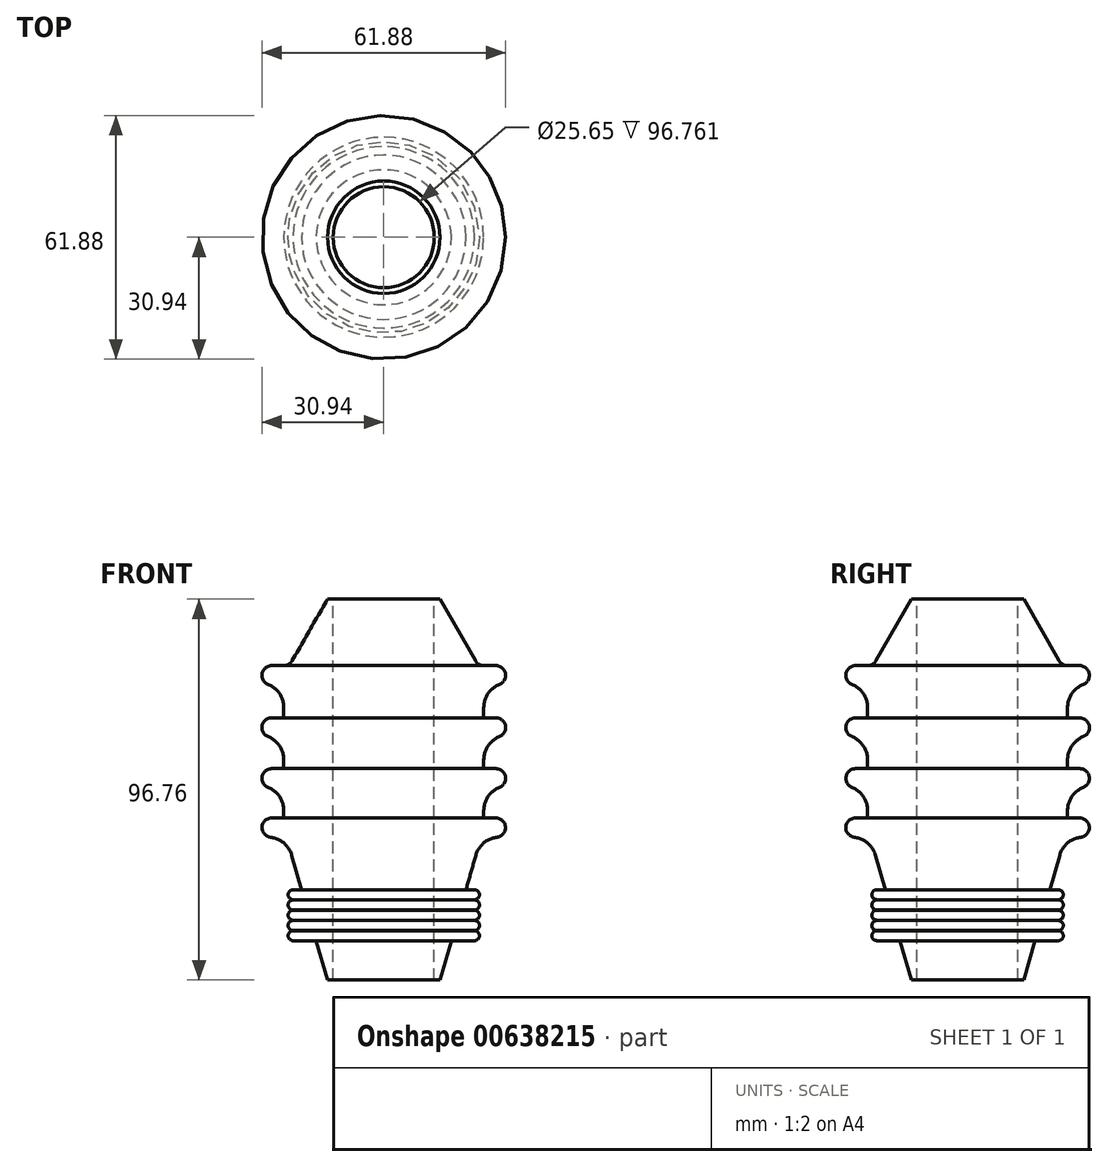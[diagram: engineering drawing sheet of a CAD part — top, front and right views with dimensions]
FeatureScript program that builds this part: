
annotation { "Feature Type Name" : "Feature", "Feature Type Description" : "" }
export const myFeature = defineFeature(function(context is Context, id is Id, definition is map)
    precondition{}
    {
        {
            var Q0;
            Q0=qCreatedBy(makeId("Front.planeOp"),FACE);
            var sketch = newSketch(context, id + "F0", { "sketchPlane" : qUnion([Q0])});
            skLineSegment(sketch, "E0", {"start": v(0, 0) * mm, "end": v(0, 96.76) * mm});
            skLineSegment(sketch, "E1", {"start": v(0, 96.76) * mm, "end": v(0, 58.06) * mm});
            skLineSegment(sketch, "E2", {"start": v(0, 0) * mm, "end": v(0, 38.7) * mm});
            skLineSegment(sketch, "E3", {"start": v(0, 96.76) * mm, "end": v(-14.29, 96.76) * mm});
            skLineSegment(sketch, "E4", {"start": v(-14.29, 96.76) * mm, "end": v(-14.29, 0) * mm});
            skLineSegment(sketch, "E5", {"start": v(-14.29, 0) * mm, "end": v(0, 0) * mm});
            skLineSegment(sketch, "E6", {"start": v(0, 96.76) * mm, "end": v(0, 77.4) * mm});
            skLineSegment(sketch, "E7", {"start": v(-25.4, 77.4) * mm, "end": v(-25.4, 38.7) * mm});
            skLineSegment(sketch, "E8", {"start": v(-25.4, 77.4) * mm, "end": v(-14.29, 96.76) * mm});
            skLineSegment(sketch, "E9", {"start": v(-25.4, 38.7) * mm, "end": v(-14.29, 0) * mm});
            skLineSegment(sketch, "E10", {"start": v(-25.4, 77.4) * mm, "end": v(-25.4, 64.14) * mm});
            skLineSegment(sketch, "E11", {"start": v(-25.4, 64.14) * mm, "end": v(-25.4, 51.24) * mm});
            skLineSegment(sketch, "E12", {"start": v(-25.4, 77.4) * mm, "end": v(-25.4, 74.95) * mm});
            skLineSegment(sketch, "E13", {"start": v(-25.4, 77.4) * mm, "end": v(-25.4, 79.87) * mm});
            skLineSegment(sketch, "E14", {"start": v(-25.4, 79.87) * mm, "end": v(0, 79.87) * mm});
            skLineSegment(sketch, "E15", {"start": v(-25.4, 64.14) * mm, "end": v(-25.4, 66.6) * mm});
            skLineSegment(sketch, "E16", {"start": v(-25.4, 64.14) * mm, "end": v(-25.4, 61.68) * mm});
            skLineSegment(sketch, "E17", {"start": v(-25.4, 61.68) * mm, "end": v(0, 61.68) * mm});
            skLineSegment(sketch, "E18", {"start": v(-25.4, 66.6) * mm, "end": v(0, 66.6) * mm});
            skLineSegment(sketch, "E19", {"start": v(-25.4, 74.95) * mm, "end": v(0, 74.95) * mm});
            skLineSegment(sketch, "E20", {"start": v(-25.4, 51.24) * mm, "end": v(-25.4, 53.7) * mm});
            skLineSegment(sketch, "E21", {"start": v(-25.4, 51.24) * mm, "end": v(-25.4, 48.77) * mm});
            skLineSegment(sketch, "E22", {"start": v(-25.4, 48.77) * mm, "end": v(0, 48.77) * mm});
            skLineSegment(sketch, "E23", {"start": v(-25.4, 53.7) * mm, "end": v(0, 53.7) * mm});
            skLineSegment(sketch, "E24", {"start": v(-25.4, 38.7) * mm, "end": v(-25.4, 41.17) * mm});
            skLineSegment(sketch, "E25", {"start": v(-25.4, 38.7) * mm, "end": v(-25.4, 36.24) * mm});
            skLineSegment(sketch, "E26", {"start": v(-25.4, 36.24) * mm, "end": v(0, 36.24) * mm});
            skLineSegment(sketch, "E27", {"start": v(-25.4, 41.17) * mm, "end": v(0, 41.17) * mm});
            skLineSegment(sketch, "E28", {"start": v(-25.4, 79.87) * mm, "end": v(-28.48, 79.87) * mm});
            skLineSegment(sketch, "E29", {"start": v(-25.4, 36.24) * mm, "end": v(-28.48, 36.24) * mm});
            skLineSegment(sketch, "E30", {"start": v(-28.48, 36.24) * mm, "end": v(-28.48, 41.17) * mm});
            skLineSegment(sketch, "E31", {"start": v(-25.4, 74.95) * mm, "end": v(-28.48, 74.95) * mm});
            skLineSegment(sketch, "E32", {"start": v(-25.4, 66.6) * mm, "end": v(-28.48, 66.6) * mm});
            skLineSegment(sketch, "E33", {"start": v(-25.4, 61.68) * mm, "end": v(-28.48, 61.68) * mm});
            skLineSegment(sketch, "E34", {"start": v(-25.4, 53.7) * mm, "end": v(-28.48, 53.7) * mm});
            skLineSegment(sketch, "E35", {"start": v(-25.4, 48.77) * mm, "end": v(-28.48, 48.77) * mm});
            skLineSegment(sketch, "E36", {"start": v(-25.4, 41.17) * mm, "end": v(-28.48, 41.17) * mm});
            skLineSegment(sketch, "E37.trimOffspring", {"start": v(-28.48, 74.95) * mm, "end": v(-28.48, 79.87) * mm});
            skLineSegment(sketch, "E38.trimOffspring", {"start": v(-28.48, 61.68) * mm, "end": v(-28.48, 66.6) * mm});
            skLineSegment(sketch, "E39.trimOffspring", {"start": v(-28.48, 48.77) * mm, "end": v(-28.48, 53.7) * mm});
            skArc(sketch, "E40", {"start": v(-28.48, 79.87) * mm, "mid": v(-30.94, 77.4) * mm, "end": v(-28.48, 74.95) * mm});
            skArc(sketch, "E41", {"start": v(-28.48, 66.6) * mm, "mid": v(-30.94, 64.14) * mm, "end": v(-28.48, 61.68) * mm});
            skArc(sketch, "E42", {"start": v(-28.48, 53.7) * mm, "mid": v(-30.94, 51.24) * mm, "end": v(-28.48, 48.77) * mm});
            skArc(sketch, "E43", {"start": v(-28.48, 41.17) * mm, "mid": v(-30.94, 38.7) * mm, "end": v(-28.48, 36.24) * mm});
            skLineSegment(sketch, "E44", {"start": v(-24.7, 36.24) * mm, "end": v(-14.29, 0) * mm});
            skLineSegment(sketch, "E45", {"start": v(-14.29, 0) * mm, "end": v(-16.02, 6.04) * mm});
            skLineSegment(sketch, "E46", {"start": v(-24.7, 36.24) * mm, "end": v(-18.26, 13.85) * mm});
            skLineSegment(sketch, "E47", {"start": v(-16.02, 6.04) * mm, "end": v(-18.26, 13.85) * mm});
            skLineSegment(sketch, "E48", {"start": v(-18.26, 13.85) * mm, "end": v(-20.5, 21.66) * mm});
            skLineSegment(sketch, "E49", {"start": v(-20.5, 21.66) * mm, "end": v(-19.76, 19.06) * mm});
            skLineSegment(sketch, "E50", {"start": v(-19.76, 19.06) * mm, "end": v(-19.01, 16.45) * mm});
            skLineSegment(sketch, "E51", {"start": v(-19.01, 16.45) * mm, "end": v(-18.26, 13.85) * mm});
            skLineSegment(sketch, "E52", {"start": v(-18.26, 13.85) * mm, "end": v(-17.52, 11.24) * mm});
            skLineSegment(sketch, "E53", {"start": v(-17.52, 11.24) * mm, "end": v(-16.77, 8.64) * mm});
            skLineSegment(sketch, "E54", {"start": v(-16.77, 8.64) * mm, "end": v(-16.02, 6.04) * mm});
            skLineSegment(sketch, "E55", {"start": v(-20.5, 21.66) * mm, "end": v(-23.05, 21.66) * mm});
            skLineSegment(sketch, "E56", {"start": v(-23.05, 21.66) * mm, "end": v(-23.05, 9.97) * mm});
            skLineSegment(sketch, "E57", {"start": v(-17.52, 11.24) * mm, "end": v(-23.05, 11.24) * mm});
            skLineSegment(sketch, "E58", {"start": v(-23.05, 11.24) * mm, "end": v(-17.52, 11.24) * mm});
            skLineSegment(sketch, "E59", {"start": v(-18.26, 13.85) * mm, "end": v(-23.05, 13.85) * mm});
            skLineSegment(sketch, "E60", {"start": v(-23.05, 13.85) * mm, "end": v(-18.26, 13.85) * mm});
            skLineSegment(sketch, "E61", {"start": v(-19.01, 16.45) * mm, "end": v(-23.05, 16.45) * mm});
            skLineSegment(sketch, "E62", {"start": v(-23.05, 16.45) * mm, "end": v(-19.01, 16.45) * mm});
            skLineSegment(sketch, "E63", {"start": v(-19.76, 19.06) * mm, "end": v(-23.05, 19.06) * mm});
            skLineSegment(sketch, "E64", {"start": v(-23.05, 19.06) * mm, "end": v(-19.76, 19.06) * mm});
            skArc(sketch, "E65", {"start": v(-23.05, 22.93) * mm, "mid": v(-24.32, 21.66) * mm, "end": v(-23.05, 20.39) * mm});
            skArc(sketch, "E66", {"start": v(-23.05, 20.33) * mm, "mid": v(-24.32, 19.06) * mm, "end": v(-23.05, 17.79) * mm});
            skArc(sketch, "E67", {"start": v(-23.05, 17.72) * mm, "mid": v(-24.32, 16.45) * mm, "end": v(-23.05, 15.18) * mm});
            skArc(sketch, "E68", {"start": v(-23.05, 15.12) * mm, "mid": v(-24.32, 13.85) * mm, "end": v(-23.05, 12.58) * mm});
            skArc(sketch, "E69", {"start": v(-23.05, 12.51) * mm, "mid": v(-24.32, 11.24) * mm, "end": v(-23.05, 9.97) * mm});
            skLineSegment(sketch, "E70", {"start": v(-23.05, 22.93) * mm, "end": v(-20.87, 22.93) * mm});
            skLineSegment(sketch, "E71", {"start": v(-23.05, 9.97) * mm, "end": v(-17.15, 9.97) * mm});
            skPoint(sketch, "E72.end.orphan", {"position": v(-23.05, 8.64) * mm});
            skPoint(sketch, "E73.start.orphan", {"position": v(-23.05, 6.04) * mm});
            skSolve(sketch);
        }
        {
            var Q0;
            Q0 = qSketchRegion(id + "F0", true);
            var Q1;
            Q1=sQuery(id+"F0.wireOp",EDGE,"E6");
            revolve(context, id + "F1", {"entities" : qUnion([Q0]), "axis" : qUnion([Q1]), "revolveType" : RevolveType.FULL});
        }
        {
            var Q0;
            Q0=makeQuery(id+"F1.opRevolve","SWEPT_EDGE",EDGE,{"disambiguationData":[OSD([sQuery(id+"F0.wireOp",EDGE,"E9"),sQuery(id+"F0.wireOp",EDGE,"E26")])]});
            var Q1;
            Q1=makeQuery(id+"F1.opRevolve","SWEPT_EDGE",EDGE,{"disambiguationData":[OSD([sQuery(id+"F0.wireOp",EDGE,"E7"),sQuery(id+"F0.wireOp",EDGE,"E21"),sQuery(id+"F0.wireOp",EDGE,"E22"),sQuery(id+"F0.wireOp",EDGE,"E35")])]});
            var Q2;
            Q2=makeQuery(id+"F1.opRevolve","SWEPT_EDGE",EDGE,{"disambiguationData":[OSD([sQuery(id+"F0.wireOp",EDGE,"E11"),sQuery(id+"F0.wireOp",EDGE,"E16"),sQuery(id+"F0.wireOp",EDGE,"E17"),sQuery(id+"F0.wireOp",EDGE,"E33")])]});
            var Q3;
            Q3=makeQuery(id+"F1.opRevolve","SWEPT_EDGE",EDGE,{"disambiguationData":[OSD([sQuery(id+"F0.wireOp",EDGE,"E10"),sQuery(id+"F0.wireOp",EDGE,"E12"),sQuery(id+"F0.wireOp",EDGE,"E19"),sQuery(id+"F0.wireOp",EDGE,"E31")])]});
            fillet(context, id + "F2", {"entities" : qUnion([Q0, Q1, Q2, Q3]), "radius" : 6.35 * mm, "tangentPropagation" : true, "allowEdgeOverflow" : false});
        }
        {
            var Q0;
            Q0=makeQuery(id+"F1.opRevolve","SWEPT_EDGE",EDGE,{"disambiguationData":[OSD([sQuery(id+"F0.wireOp",EDGE,"E8"),sQuery(id+"F0.wireOp",EDGE,"E14")])]});
            fillet(context, id + "F3", {"entities" : qUnion([Q0]), "radius" : 2.54 * mm, "tangentPropagation" : true, "allowEdgeOverflow" : false});
        }
        {
            var Q0;
            Q0=makeQuery(id+"F1.opRevolve","SWEPT_FACE",FACE,{"disambiguationData":[OSD([sQuery(id+"F0.wireOp",EDGE,"E3")])]});
            var sketch = newSketch(context, id + "F4", { "sketchPlane" : qUnion([Q0])});
            skCircle(sketch, "E74", {"center": v(0, 0) * mm, "radius": 12.83 * mm});
            skSolve(sketch);
        }
        {
            var Q0;
            Q0 = qSketchRegion(id + "F4", true);
            extrude(context, id + "F5", {"entities" : qUnion([Q0]), "operationType" : NewBodyOperationType.REMOVE, "endBound" : BoundingType.THROUGH_ALL, "oppositeDirection" : true, "depth" : 25.4 * mm, "offsetDistance" : 25.4 * mm});
        }
    });
